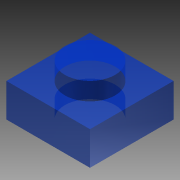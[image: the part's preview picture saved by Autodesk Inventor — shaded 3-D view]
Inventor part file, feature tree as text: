
AUTODESK INVENTOR PART (.ipt)
format: ipt  version: 2013 (Build 170138000, 138)  size: 106,496 bytes
history: native  units: mm
features: extrude x3, sketch x1, pattern_linear x1
ambient origin geometry x8: Origin, YZ Plane, XZ Plane, XY Plane, X Axis, Y Axis, Z Axis, Center Point
bodies: Solid1 (feature_tree)
feature tree (5):
  sketch  "Sketch1"  dims[d0=8.0mm d1=8.0mm d2=4.8mm d3=3.2mm d4=0.0mm d5=4.9mm d6=0.0mm d7=1.7mm d8=0.0mm d9=10.0mm d11=8.0mm d22=10.0mm d24=8.0mm]
  extrude  "Extrusion1"  Depth=8.0mm
  extrude  "Extrusion2"  Depth=4.8mm
  extrude  "Extrusion3"  Depth=3.2mm TaperAngle=0.0deg
  pattern_linear  "Rectangular Pattern1"  Spacing1=4.9mm  [1 undecoded]
note: 1 required parameter value undecoded (feature->parameter linkage not recoverable at this tier; creation-order binding heuristic only, values carry confidence <= 0.55)
